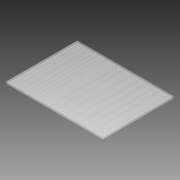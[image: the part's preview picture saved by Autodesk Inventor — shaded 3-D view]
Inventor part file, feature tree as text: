
AUTODESK INVENTOR PART (.ipt)
format: ipt  version: 2012 (Build 160160000, 160)  size: 281,088 bytes
history: native  units: in
note: dims shown in document units (in); Inventor stores cm internally (conversion verified against a paired STEP export)
features: extrude x1, sketch x1
ambient origin geometry x8: Origin, YZ Plane, XZ Plane, XY Plane, X Axis, Y Axis, Z Axis, Center Point
bodies: Solid1 (feature_tree)
feature tree (2):
  extrude  "Extrusion1"  Depth=0.25in
  sketch  "Sketch1"  dims[d0=12.02in d1=0.25in d2=0.0201in d3=0.02in d4=0.02in d5=0.23in d6=18.8976in d8=0.25in d9=0.3937in d11=1.0in d13=8.875in d14=0.0in]
